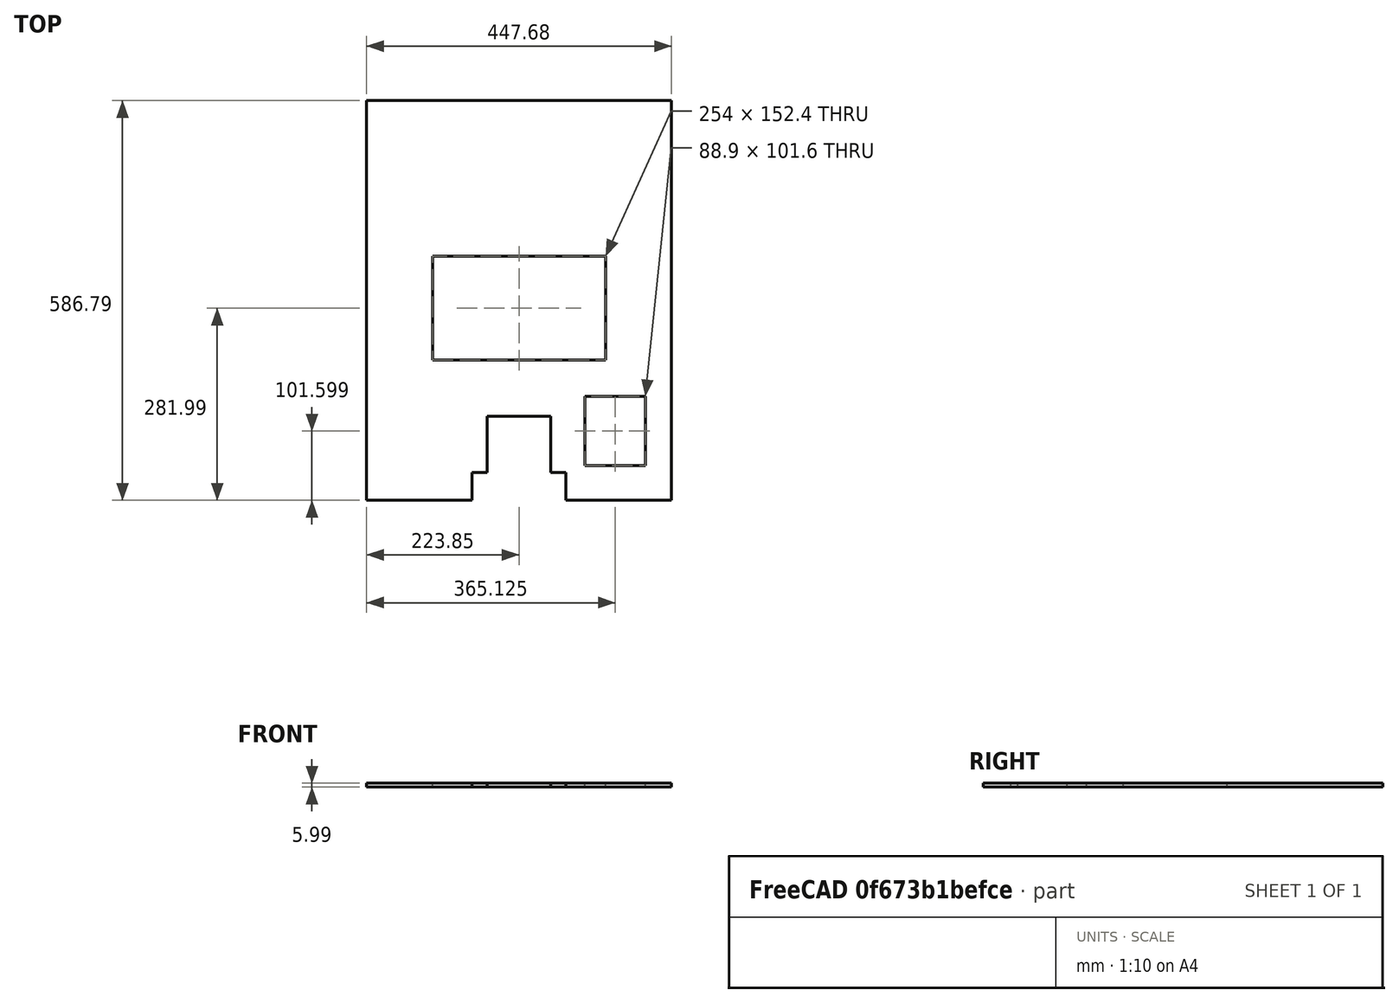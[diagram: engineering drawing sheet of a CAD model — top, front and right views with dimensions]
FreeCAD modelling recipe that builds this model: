
FCSTD DOCUMENT  (FreeCAD 0.19R24267 (Git))
Label: Inv1-P15
License: All rights reserved
LicenseURL: http://en.wikipedia.org/wiki/All_rights_reserved
objects: TechDraw::DrawViewDimension×17, TechDraw::DrawProjGroupItem×2, TechDraw::DrawHatch×2, TechDraw::DrawViewAnnotation×2, Sketcher::SketchObject×1, Part::Extrusion×1, TechDraw::DrawSVGTemplate×1, TechDraw::DrawProjGroup×1, TechDraw::DrawPage×1
note: 2 computed .brp shape members not serialized (recipe doc carries the construction recipe); baked Part::Feature solids carry a one-line shape summary decoded from their .brp

FEATURE [Sketcher::SketchObject] Sketch
  FullyConstrained = true
  sketch-geometry (20):
    g0: LineSegment StartX=0 StartY=0 StartZ=0 EndX=447.675 EndY=0 EndZ=0
    g1: LineSegment StartX=447.675 StartY=0 StartZ=0 EndX=447.675 EndY=-586.791 EndZ=0
    g2: LineSegment StartX=447.675 StartY=-586.791 StartZ=0 EndX=292.735 EndY=-586.791 EndZ=0
    g3: LineSegment StartX=292.735 StartY=-586.791 StartZ=0 EndX=292.735 EndY=-546.1 EndZ=0
    g4: LineSegment StartX=292.735 StartY=-546.1 StartZ=0 EndX=270.383 EndY=-546.1 EndZ=0
    g5: LineSegment StartX=270.383 StartY=-546.1 StartZ=0 EndX=270.383 EndY=-463.55 EndZ=0
    g6: LineSegment StartX=270.383 StartY=-463.55 StartZ=0 EndX=177.292 EndY=-463.55 EndZ=0
    g7: LineSegment StartX=177.292 StartY=-463.55 StartZ=0 EndX=177.292 EndY=-546.1 EndZ=0
    g8: LineSegment StartX=177.292 StartY=-546.1 StartZ=0 EndX=154.94 EndY=-546.1 EndZ=0
    g9: LineSegment StartX=154.94 StartY=-546.1 StartZ=0 EndX=154.94 EndY=-586.791 EndZ=0
    g10: LineSegment StartX=154.94 StartY=-586.791 StartZ=0 EndX=0 EndY=-586.791 EndZ=0
    g11: LineSegment StartX=0 StartY=0 StartZ=0 EndX=0 EndY=-586.791 EndZ=0
    g12: LineSegment StartX=320.675 StartY=-434.391 StartZ=0 EndX=409.575 EndY=-434.391 EndZ=0
    g13: LineSegment StartX=409.575 StartY=-434.391 StartZ=0 EndX=409.575 EndY=-535.991 EndZ=0
    g14: LineSegment StartX=409.575 StartY=-535.991 StartZ=0 EndX=320.675 EndY=-535.991 EndZ=0
    g15: LineSegment StartX=320.675 StartY=-535.991 StartZ=0 EndX=320.675 EndY=-434.391 EndZ=0
    g16: LineSegment StartX=96.8502 StartY=-228.6 StartZ=0 EndX=350.85 EndY=-228.6 EndZ=0
    g17: LineSegment StartX=350.85 StartY=-228.6 StartZ=0 EndX=350.85 EndY=-381 EndZ=0
    g18: LineSegment StartX=350.85 StartY=-381 StartZ=0 EndX=96.8502 EndY=-381 EndZ=0
    g19: LineSegment StartX=96.8502 StartY=-381 StartZ=0 EndX=96.8502 EndY=-228.6 EndZ=0
  constraints (59):
    c: Coincident(g0,g-1)
    c: Horizontal(g0)
    c: Coincident(g1,g0)
    c: Vertical(g1)
    c: Coincident(g2,g1)
    c: Horizontal(g2)
    c: Coincident(g3,g2)
    c: Vertical(g3)
    c: Coincident(g4,g3)
    c: Horizontal(g4)
    c: Coincident(g5,g4)
    c: Vertical(g5)
    c: Coincident(g6,g5)
    c: Horizontal(g6)
    c: Coincident(g7,g6)
    c: Vertical(g7)
    c: Coincident(g8,g7)
    c: Horizontal(g8)
    c: Coincident(g9,g8)
    c: Vertical(g9)
    c: Coincident(g10,g9)
    c: Horizontal(g10)
    c: Coincident(g11,g0)
    c: Coincident(g11,g10)
    c: Vertical(g11)
    c: Distance(g11) = 586.791
    c: Distance(g0) = 447.675
    c: Distance(g10) = 154.94
    c: Equal(g2,g10)
    c: Distance(g8) = 22.352
    c: Equal(g8,g4)
    c: Distance(g9) = 40.6908
    c: Equal(g3,g9)
    c: Distance(g7) = 82.55
    c: Equal(g5,g7)
    c: Coincident(g12,g13)
    c: Coincident(g13,g14)
    c: Coincident(g14,g15)
    c: Coincident(g15,g12)
    c: Horizontal(g12)
    c: Horizontal(g14)
    c: Vertical(g13)
    c: Vertical(g15)
    c: Distance(g12) = 88.9
    c: Distance(g13) = 101.6
    c: Distance(g13,g2) = 50.8
    c: Distance(g13,g1) = 38.1
    c: Coincident(g16,g17)
    c: Coincident(g17,g18)
    c: Coincident(g18,g19)
    c: Coincident(g19,g16)
    c: Horizontal(g16)
    c: Horizontal(g18)
    c: Vertical(g17)
    c: Vertical(g19)
    c: Distance(g18) = 254
    c: Distance(g16,g11) = 96.8502
    c: Distance(g17) = 152.4
    c: Distance(g16,g0) = 228.6
FEATURE [Part::Extrusion] Extrude
  Base = -> Sketch
  Dir = (0,0,1)
  DirMode = 2
  FaceMakerClass = Part::FaceMakerBullseye
  LengthFwd = 5.9944
  LengthRev = 0
  Solid = true
  Symmetric = false
FEATURE [TechDraw::DrawSVGTemplate] Template
  Height = 215.9
  Orientation = 1
  Width = 279.4
FEATURE [TechDraw::DrawProjGroupItem] ProjItem  label="Front"
  CoarseView = false
  Direction = (0,0,1)
  Focus = 100
  HardHidden = false
  IsoCount = 0
  IsoHidden = false
  IsoVisible = false
  LockPosition = true
  Perspective = false
  Rotation = 0
  RotationVector = (1,0,0)
  Scale = 0.2
  ScaleType = 2
  SeamHidden = false
  SeamVisible = true
  SmoothHidden = false
  SmoothVisible = true
  Source = -> [Extrude]
  Type = 0
  X = 0
  XDirection = (1,0,0)
  Y = 0
FEATURE [TechDraw::DrawProjGroupItem] ProjItem001  label="Left"
  CoarseView = false
  Direction = (-1,0,1e-16)
  Focus = 100
  HardHidden = false
  IsoCount = 0
  IsoHidden = false
  IsoVisible = false
  LockPosition = false
  Perspective = false
  Rotation = 0
  RotationVector = (1,0,0)
  ScaleType = 2
  SeamHidden = false
  SeamVisible = true
  SmoothHidden = false
  SmoothVisible = true
  Source = -> [Extrude]
  Type = 1
  X = 87.9397
  XDirection = (1e-16,0,1)
  Y = 0
FEATURE [TechDraw::DrawProjGroup] ProjGroup
  Anchor = -> ProjItem
  AutoDistribute = true
  LockPosition = false
  ProjectionType = 0
  Rotation = 0
  Scale = 0.2
  ScaleType = 2
  Source = -> [Extrude]
  Views = -> [ProjItem,ProjItem001]
  X = 123.37
  Y = 108.391
  spacingX = 15.0114
  spacingY = 15.0114
FEATURE [TechDraw::DrawHatch] Hatch  label="HatchF0"
  HatchPattern = <path>
  Source = -> ProjItem [Face0]
FEATURE [TechDraw::DrawHatch] Hatch001  label="Hatch001F0"
  HatchPattern = <path>
  Source = -> ProjItem001 [Face0]
FEATURE [TechDraw::DrawViewDimension] Dimension
  Arbitrary = false
  ArbitraryTolerances = false
  EqualTolerance = true
  FormatSpec = %.3f
  FormatSpecOverTolerance = %+.3f
  FormatSpecUnderTolerance = %+.3f
  Inverted = false
  LockPosition = false
  MeasureType = 1
  OverTolerance = 0
  References2D = -> [ProjItem]
  Rotation = 0
  ScaleType = 0
  TheoreticalExact = false
  Type = 2
  UnderTolerance = 0
  X = -58.4775
  Y = 0
FEATURE [TechDraw::DrawViewDimension] Dimension001
  Arbitrary = false
  ArbitraryTolerances = false
  EqualTolerance = true
  FormatSpec = %.3f
  FormatSpecOverTolerance = %+.3f
  FormatSpecUnderTolerance = %+.3f
  Inverted = false
  LockPosition = false
  MeasureType = 1
  OverTolerance = 0
  References2D = -> [ProjItem]
  Rotation = 0
  ScaleType = 0
  TheoreticalExact = false
  Type = 2
  UnderTolerance = 0
  X = 31.0767
  Y = -1.55769
FEATURE [TechDraw::DrawViewDimension] Dimension002
  Arbitrary = false
  ArbitraryTolerances = false
  EqualTolerance = true
  FormatSpec = %.3f
  FormatSpecOverTolerance = %+.3f
  FormatSpecUnderTolerance = %+.3f
  Inverted = false
  LockPosition = false
  MeasureType = 1
  OverTolerance = 0
  References2D = -> [ProjItem]
  Rotation = 0
  ScaleType = 0
  TheoreticalExact = false
  Type = 1
  UnderTolerance = 0
  X = 0.00254
  Y = 25.5499
FEATURE [TechDraw::DrawViewDimension] Dimension003
  Arbitrary = false
  ArbitraryTolerances = false
  EqualTolerance = true
  FormatSpec = %.3f
  FormatSpecOverTolerance = %+.3f
  FormatSpecUnderTolerance = %+.3f
  Inverted = false
  LockPosition = false
  MeasureType = 1
  OverTolerance = 0
  References2D = -> [ProjItem]
  Rotation = 0
  ScaleType = 0
  TheoreticalExact = false
  Type = 2
  UnderTolerance = 0
  X = 13.5213
  Y = -36.4434
FEATURE [TechDraw::DrawViewDimension] Dimension004
  Arbitrary = false
  ArbitraryTolerances = false
  EqualTolerance = true
  FormatSpec = %.3f
  FormatSpecOverTolerance = %+.3f
  FormatSpecUnderTolerance = %+.3f
  Inverted = false
  LockPosition = false
  MeasureType = 1
  OverTolerance = 0
  References2D = -> [ProjItem]
  Rotation = 0
  ScaleType = 0
  TheoreticalExact = false
  Type = 1
  UnderTolerance = 0
  X = 28.4703
  Y = -20.3237
FEATURE [TechDraw::DrawViewDimension] Dimension005
  Arbitrary = false
  ArbitraryTolerances = false
  EqualTolerance = true
  FormatSpec = %.3f
  FormatSpecOverTolerance = %+.3f
  FormatSpecUnderTolerance = %+.3f
  Inverted = false
  LockPosition = false
  MeasureType = 1
  OverTolerance = 0
  References2D = -> [ProjItem]
  Rotation = 0
  ScaleType = 0
  TheoreticalExact = false
  Type = 2
  UnderTolerance = 0
  X = 30.7946
  Y = 35.6062
FEATURE [TechDraw::DrawViewDimension] Dimension006
  Arbitrary = false
  ArbitraryTolerances = false
  EqualTolerance = true
  FormatSpec = %.3f
  FormatSpecOverTolerance = %+.3f
  FormatSpecUnderTolerance = %+.3f
  Inverted = false
  LockPosition = false
  MeasureType = 1
  OverTolerance = 0
  References2D = -> [ProjItem]
  Rotation = 0
  ScaleType = 0
  TheoreticalExact = false
  Type = 1
  UnderTolerance = 0
  X = -34.8815
  Y = 25.5454
FEATURE [TechDraw::DrawViewDimension] Dimension007
  Arbitrary = false
  ArbitraryTolerances = false
  EqualTolerance = true
  FormatSpec = %.3f
  FormatSpecOverTolerance = %+.3f
  FormatSpecUnderTolerance = %+.3f
  Inverted = false
  LockPosition = false
  MeasureType = 1
  OverTolerance = 0
  References2D = -> [ProjItem]
  Rotation = 0
  ScaleType = 0
  TheoreticalExact = false
  Type = 2
  UnderTolerance = 0
  X = 25.6758
  Y = -73.4646
FEATURE [TechDraw::DrawViewDimension] Dimension008
  Arbitrary = false
  ArbitraryTolerances = false
  EqualTolerance = true
  FormatSpec = %.3f
  FormatSpecOverTolerance = %+.3f
  FormatSpecUnderTolerance = %+.3f
  Inverted = false
  LockPosition = false
  MeasureType = 1
  OverTolerance = 0
  References2D = -> [ProjItem]
  Rotation = 0
  ScaleType = 0
  TheoreticalExact = false
  Type = 1
  UnderTolerance = 0
  X = 58.8831
  Y = -29.4649
FEATURE [TechDraw::DrawViewDimension] Dimension009
  Arbitrary = false
  ArbitraryTolerances = false
  EqualTolerance = true
  FormatSpec = %.3f
  FormatSpecOverTolerance = %+.3f
  FormatSpecUnderTolerance = %+.3f
  Inverted = false
  LockPosition = false
  MeasureType = 1
  OverTolerance = 0
  References2D = -> [ProjItem]
  Rotation = 0
  ScaleType = 0
  TheoreticalExact = false
  Type = 1
  UnderTolerance = 0
  X = 27.895
  Y = -82.833
FEATURE [TechDraw::DrawViewDimension] Dimension010
  Arbitrary = false
  ArbitraryTolerances = false
  EqualTolerance = true
  FormatSpec = %.3f
  FormatSpecOverTolerance = %+.3f
  FormatSpecUnderTolerance = %+.3f
  Inverted = false
  LockPosition = false
  MeasureType = 1
  OverTolerance = 0
  References2D = -> [ProjItem]
  Rotation = 0
  ScaleType = 0
  TheoreticalExact = false
  Type = 1
  UnderTolerance = 0
  X = -27.5947
  Y = -83.3478
FEATURE [TechDraw::DrawViewDimension] Dimension011
  Arbitrary = false
  ArbitraryTolerances = false
  EqualTolerance = true
  FormatSpec = %.3f
  FormatSpecOverTolerance = %+.3f
  FormatSpecUnderTolerance = %+.3f
  Inverted = false
  LockPosition = false
  MeasureType = 1
  OverTolerance = 0
  References2D = -> [ProjItem]
  Rotation = 0
  ScaleType = 0
  TheoreticalExact = false
  Type = 1
  UnderTolerance = 0
  X = -1.93611
  Y = -73.1667
FEATURE [TechDraw::DrawViewDimension] Dimension012
  Arbitrary = false
  ArbitraryTolerances = false
  EqualTolerance = true
  FormatSpec = %.3f
  FormatSpecOverTolerance = %+.3f
  FormatSpecUnderTolerance = %+.3f
  Inverted = false
  LockPosition = false
  MeasureType = 1
  OverTolerance = 0
  References2D = -> [ProjItem]
  Rotation = 0
  ScaleType = 0
  TheoreticalExact = false
  Type = 1
  UnderTolerance = 0
  X = 0.559593
  Y = -23.6784
FEATURE [TechDraw::DrawViewDimension] Dimension013
  Arbitrary = false
  ArbitraryTolerances = false
  EqualTolerance = true
  FormatSpec = %.3f
  FormatSpecOverTolerance = %+.3f
  FormatSpecUnderTolerance = %+.3f
  Inverted = false
  LockPosition = false
  MeasureType = 1
  OverTolerance = 0
  References2D = -> [ProjItem]
  Rotation = 0
  ScaleType = 0
  TheoreticalExact = false
  Type = 1
  UnderTolerance = 0
  X = 0.015001
  Y = -63.6666
FEATURE [TechDraw::DrawViewDimension] Dimension014
  Arbitrary = false
  ArbitraryTolerances = false
  EqualTolerance = true
  FormatSpec = %.3f
  FormatSpecOverTolerance = %+.3f
  FormatSpecUnderTolerance = %+.3f
  Inverted = false
  LockPosition = false
  MeasureType = 1
  OverTolerance = 0
  References2D = -> [ProjItem]
  Rotation = 0
  ScaleType = 0
  TheoreticalExact = false
  Type = 2
  UnderTolerance = 0
  X = -35.7078
  Y = -38.8237
FEATURE [TechDraw::DrawViewDimension] Dimension015
  Arbitrary = false
  ArbitraryTolerances = false
  EqualTolerance = true
  FormatSpec = %.3f
  FormatSpecOverTolerance = %+.3f
  FormatSpecUnderTolerance = %+.3f
  Inverted = false
  LockPosition = false
  MeasureType = 1
  OverTolerance = 0
  References2D = -> [ProjItem]
  Rotation = 0
  ScaleType = 0
  TheoreticalExact = false
  Type = 2
  UnderTolerance = 0
  X = -29.8845
  Y = -21.0011
FEATURE [TechDraw::DrawViewDimension] Dimension016
  Arbitrary = false
  ArbitraryTolerances = false
  EqualTolerance = true
  FormatSpec = %.3f
  FormatSpecOverTolerance = %+.3f
  FormatSpecUnderTolerance = %+.3f
  Inverted = false
  LockPosition = false
  MeasureType = 1
  OverTolerance = 0
  References2D = -> [ProjItem001]
  Rotation = 0
  ScaleType = 0
  TheoreticalExact = false
  Type = 1
  UnderTolerance = 0
  X = 14.0989
  Y = 51.25
FEATURE [TechDraw::DrawViewAnnotation] Annotation
  Font = osifont
  LineSpace = 80
  LockPosition = false
  MaxWidth = -1
  Rotation = 0
  ScaleType = 0
  Text = Figure S1 (Inverted 1) |  Panel 15 [front] | Quantity: 1
  TextSize = 5.0038
  TextStyle = 0
  X = 31.9554
  Y = 195.58
FEATURE [TechDraw::DrawViewAnnotation] Annotation002
  Font = osifont
  LineSpace = 80
  LockPosition = false
  MaxWidth = -1
  Rotation = 0
  ScaleType = 0
  Text = Units: Inches
  TextSize = 5.0038
  TextStyle = 0
  X = 259.08
  Y = 5.08
FEATURE [TechDraw::DrawPage] Page
  KeepUpdated = true
  NextBalloonIndex = 1
  ProjectionType = 0
  Template = -> Template
  Views = -> [ProjGroup,Dimension,Dimension001,Dimension002,Dimension003,Dimension004,Dimension005,Dimension006,Dimension007,Dimension008,Dimension009,Dimension010,Dimension011,Dimension012,Dimension013,Dimension014,Dimension015,Dimension016,Annotation,Annotation002]
note: 2 file-system paths scrubbed to <path> (originals preserved in the JSON sidecar)
